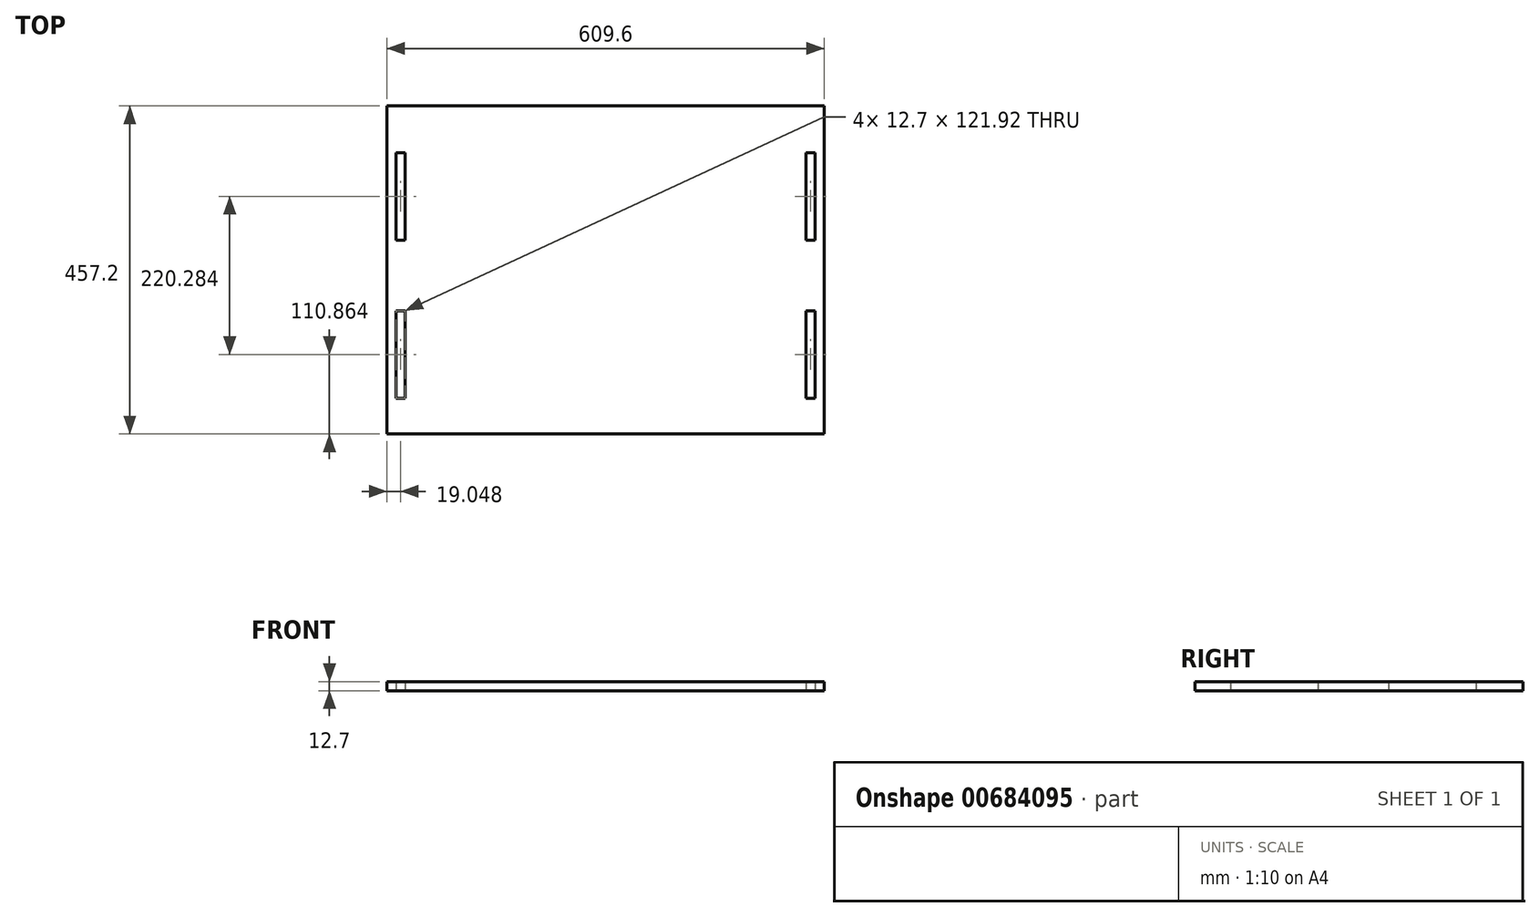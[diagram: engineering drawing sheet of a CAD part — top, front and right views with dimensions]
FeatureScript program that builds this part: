
annotation { "Feature Type Name" : "Feature", "Feature Type Description" : "" }
export const myFeature = defineFeature(function(context is Context, id is Id, definition is map)
    precondition{}
    {
        {
            var Q0;
            Q0=qCreatedBy(makeId("Top.planeOp"),FACE);
            var sketch = newSketch(context, id + "F0", { "sketchPlane" : qUnion([Q0])});
            skLineSegment(sketch, "E0.bottom", {"start": v(-304.02, 273.73) * mm, "end": v(305.58, 273.73) * mm});
            skLineSegment(sketch, "E0.top", {"start": v(-304.02, -183.47) * mm, "end": v(305.58, -183.47) * mm});
            skLineSegment(sketch, "E0.left", {"start": v(-304.02, 273.73) * mm, "end": v(-304.02, -183.47) * mm});
            skLineSegment(sketch, "E0.right", {"start": v(305.58, 273.73) * mm, "end": v(305.58, -183.47) * mm});
            skSolve(sketch);
        }
        {
            var Q0;
            Q0=qCreatedBy(makeId("Top.planeOp"),FACE);
            var sketch = newSketch(context, id + "F1", { "sketchPlane" : qUnion([Q0])});
            skLineSegment(sketch, "E1.bottom", {"start": v(-291.32, 208.64) * mm, "end": v(-278.62, 208.64) * mm});
            skLineSegment(sketch, "E1.top", {"start": v(-291.32, 86.72) * mm, "end": v(-278.62, 86.72) * mm});
            skLineSegment(sketch, "E1.left", {"start": v(-291.32, 208.64) * mm, "end": v(-291.32, 86.72) * mm});
            skLineSegment(sketch, "E1.right", {"start": v(-278.62, 208.64) * mm, "end": v(-278.62, 86.72) * mm});
            skLineSegment(sketch, "E2.bottom", {"start": v(-291.32, -11.65) * mm, "end": v(-278.62, -11.65) * mm});
            skLineSegment(sketch, "E2.top", {"start": v(-291.32, -133.57) * mm, "end": v(-278.62, -133.57) * mm});
            skLineSegment(sketch, "E2.left", {"start": v(-291.32, -11.65) * mm, "end": v(-291.32, -133.57) * mm});
            skLineSegment(sketch, "E2.right", {"start": v(-278.62, -11.65) * mm, "end": v(-278.62, -133.57) * mm});
            skLineSegment(sketch, "E3.bottom", {"start": v(280.18, 208.64) * mm, "end": v(292.88, 208.64) * mm});
            skLineSegment(sketch, "E3.top", {"start": v(280.18, 86.72) * mm, "end": v(292.88, 86.72) * mm});
            skLineSegment(sketch, "E3.left", {"start": v(280.18, 208.64) * mm, "end": v(280.18, 86.72) * mm});
            skLineSegment(sketch, "E3.right", {"start": v(292.88, 208.64) * mm, "end": v(292.88, 86.72) * mm});
            skLineSegment(sketch, "E4.bottom", {"start": v(280.18, -133.57) * mm, "end": v(292.88, -133.57) * mm});
            skLineSegment(sketch, "E4.top", {"start": v(280.18, -11.65) * mm, "end": v(292.88, -11.65) * mm});
            skLineSegment(sketch, "E4.left", {"start": v(280.18, -133.57) * mm, "end": v(280.18, -11.65) * mm});
            skLineSegment(sketch, "E4.right", {"start": v(292.88, -133.57) * mm, "end": v(292.88, -11.65) * mm});
            skSolve(sketch);
        }
        {
            var Q0;
            Q0 = qSketchRegion(id + "F0", true);
            extrude(context, id + "F2", {"entities" : qUnion([Q0]), "depth" : 12.7 * mm, "offsetDistance" : 25.4 * mm});
        }
        {
            var Q0;
            Q0 = qSketchRegion(id + "F1", true);
            extrude(context, id + "F3", {"entities" : qUnion([Q0]), "operationType" : NewBodyOperationType.REMOVE, "depth" : 12.7 * mm, "offsetDistance" : 25.4 * mm});
        }
    });
